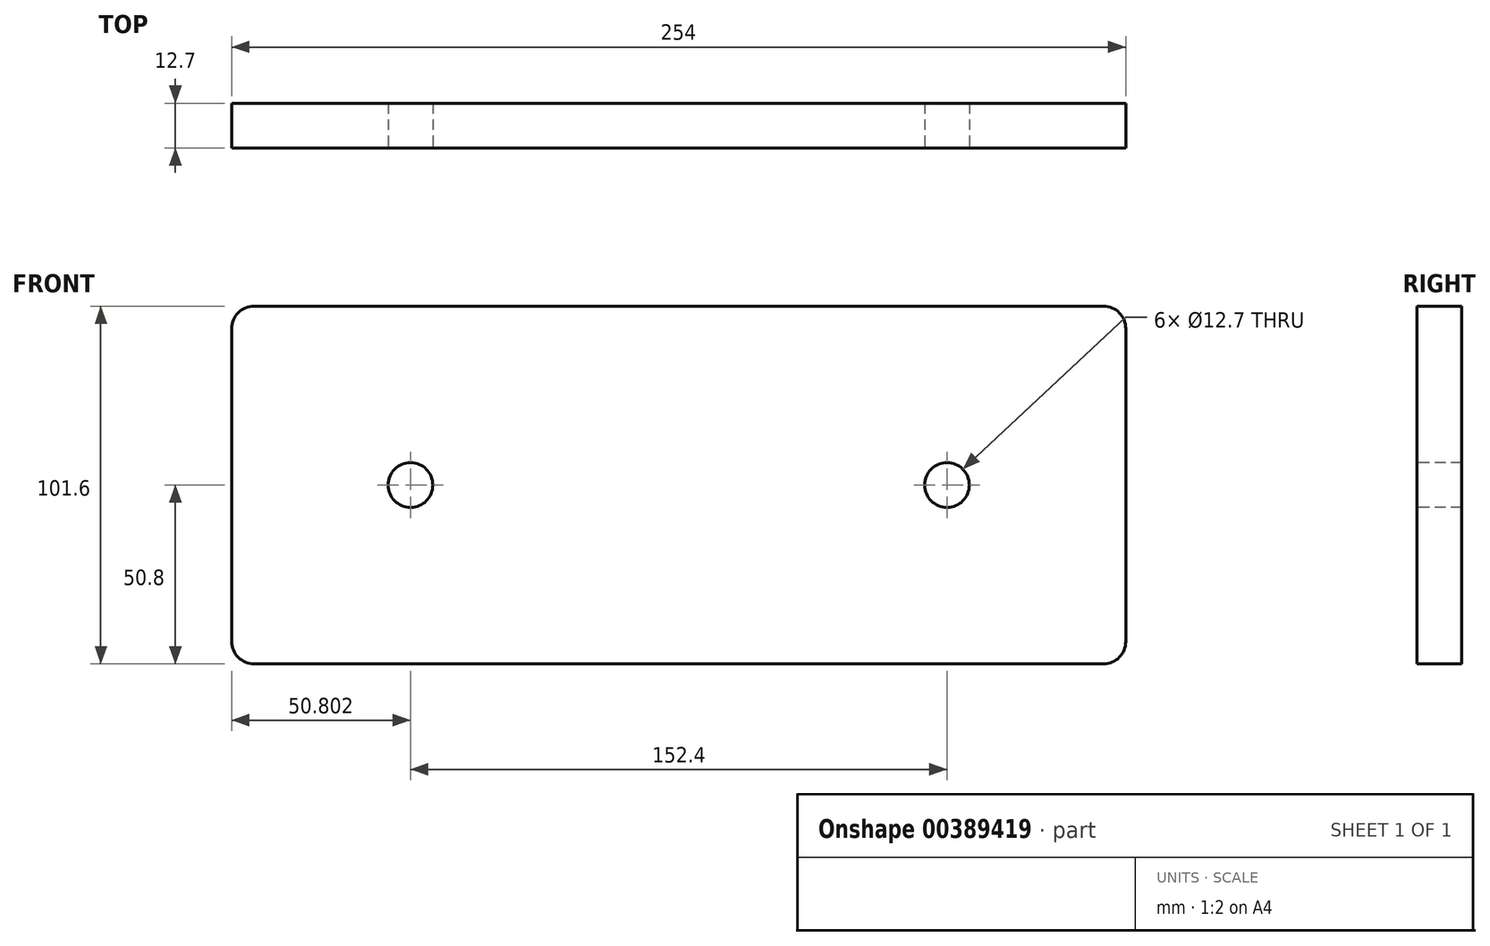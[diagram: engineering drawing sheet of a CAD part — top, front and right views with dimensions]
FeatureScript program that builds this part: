
annotation { "Feature Type Name" : "Feature", "Feature Type Description" : "" }
export const myFeature = defineFeature(function(context is Context, id is Id, definition is map)
    precondition{}
    {
        {
            var Q0;
            Q0=qCreatedBy(makeId("Front.planeOp"),FACE);
            var sketch = newSketch(context, id + "F0", { "sketchPlane" : qUnion([Q0])});
            skLineSegment(sketch, "E0.bottom", {"start": v(-116.67, 0) * mm, "end": v(137.33, 0) * mm});
            skLineSegment(sketch, "E0.top", {"start": v(-116.67, 101.6) * mm, "end": v(137.33, 101.6) * mm});
            skLineSegment(sketch, "E0.left", {"start": v(-116.67, 0) * mm, "end": v(-116.67, 101.6) * mm});
            skLineSegment(sketch, "E0.right", {"start": v(137.33, 0) * mm, "end": v(137.33, 101.6) * mm});
            skSolve(sketch);
        }
        {
            var Q0;
            Q0 = qSketchRegion(id + "F0", true);
            extrude(context, id + "F1", {"entities" : qUnion([Q0]), "depth" : 12.7 * mm});
        }
        {
            var Q0;
            Q0=makeQuery(id+"F1.opExtrude","CAP_FACE",FACE,{"disambiguationData":[OSD([sQuery(id+"F0.wireOp",EDGE,"E0.bottom"),sQuery(id+"F0.wireOp",EDGE,"E0.top"),sQuery(id+"F0.wireOp",EDGE,"E0.left"),sQuery(id+"F0.wireOp",EDGE,"E0.right")])],"isStart":false});
            var sketch = newSketch(context, id + "F2", { "sketchPlane" : qUnion([Q0])});
            skPoint(sketch, "E1", {"position": v(-65.87, 50.8) * mm});
            skPoint(sketch, "E2", {"position": v(86.53, 50.8) * mm});
            skSolve(sketch);
        }
        {
            var Q0;
            Q0=sQuery(id+"F2.wireOp",VERTEX,"E1");
            var Q1;
            Q1=sQuery(id+"F2.wireOp",VERTEX,"E2");
            var Q2;
            Q2=makeQuery(id+"F1.opExtrude","SWEPT_BODY",BODY,{"disambiguationData":[OSD([sQuery(id+"F0.wireOp",EDGE,"E0.bottom"),sQuery(id+"F0.wireOp",EDGE,"E0.top"),sQuery(id+"F0.wireOp",EDGE,"E0.left"),sQuery(id+"F0.wireOp",EDGE,"E0.right")])]});
            hole(context, id + "F3", {"style" : HoleStyle.SIMPLE, "endStyle" : HoleEndStyle.THROUGH, "holeDiameter" : 12.7 * mm, "isTappedThrough" : true, "tappedDepth" : 12.7 * mm, "tapClearance" : 3, "locations" : qUnion([Q0, Q1]), "scope" : qUnion([Q2])});
        }
        {
            var Q0;
            Q0=makeQuery(id+"F1.opExtrude","SWEPT_EDGE",EDGE,{"disambiguationData":[OSD([sQuery(id+"F0.wireOp",EDGE,"E0.top"),sQuery(id+"F0.wireOp",EDGE,"E0.right")])]});
            var Q1;
            Q1=makeQuery(id+"F1.opExtrude","SWEPT_EDGE",EDGE,{"disambiguationData":[OSD([sQuery(id+"F0.wireOp",EDGE,"E0.top"),sQuery(id+"F0.wireOp",EDGE,"E0.left")])]});
            var Q2;
            Q2=makeQuery(id+"F1.opExtrude","SWEPT_EDGE",EDGE,{"disambiguationData":[OSD([sQuery(id+"F0.wireOp",EDGE,"E0.bottom"),sQuery(id+"F0.wireOp",EDGE,"E0.right")])]});
            var Q3;
            Q3=makeQuery(id+"F1.opExtrude","SWEPT_EDGE",EDGE,{"disambiguationData":[OSD([sQuery(id+"F0.wireOp",EDGE,"E0.bottom"),sQuery(id+"F0.wireOp",EDGE,"E0.left")])]});
            fillet(context, id + "F4", {"entities" : qUnion([Q0, Q1, Q2, Q3]), "radius" : 6.35 * mm, "tangentPropagation" : true, "allowEdgeOverflow" : false});
        }
    });
